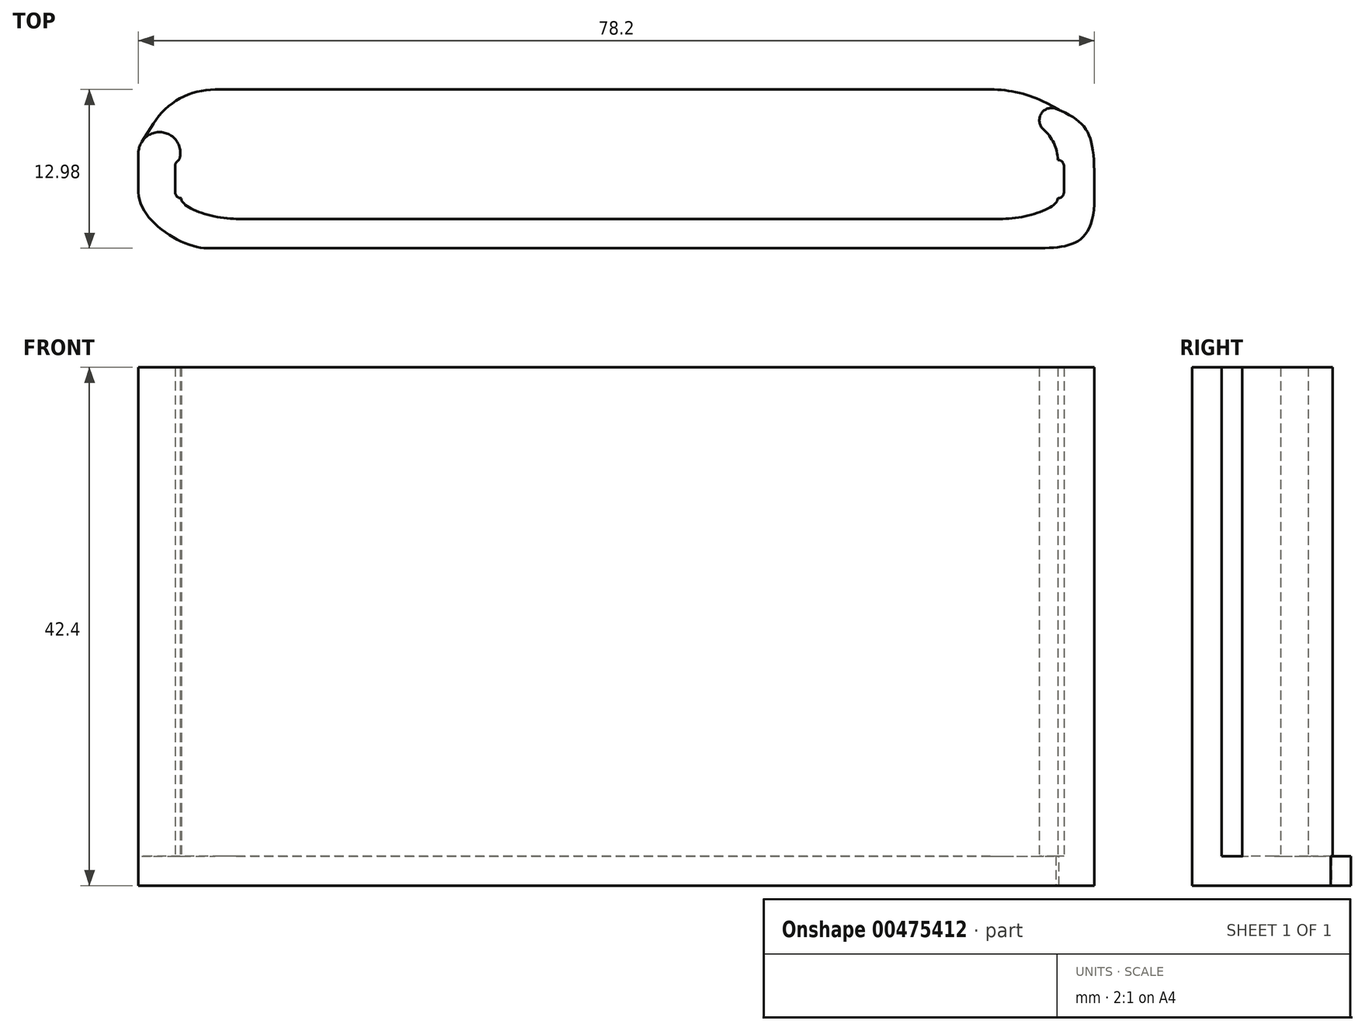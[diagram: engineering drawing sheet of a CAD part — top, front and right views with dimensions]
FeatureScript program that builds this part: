
annotation { "Feature Type Name" : "Feature", "Feature Type Description" : "" }
export const myFeature = defineFeature(function(context is Context, id is Id, definition is map)
    precondition{}
    {
        {
            var Q0;
            Q0=qCreatedBy(makeId("Top.planeOp"),FACE);
            var sketch = newSketch(context, id + "F0", { "sketchPlane" : qUnion([Q0])});
            skLineSegment(sketch, "E0", {"start": v(0, 15.59) * mm, "end": v(0, -8.36) * mm, "construction": true});
            skLineSegment(sketch, "E1", {"start": v(-58.12, 0) * mm, "end": v(52.13, 0) * mm, "construction": true});
            skLineSegment(sketch, "E2", {"start": v(0, 1.57) * mm, "end": v(35.85, 1.57) * mm});
            skLineSegment(sketch, "E3", {"start": v(36.35, 1.07) * mm, "end": v(36.35, -1.07) * mm});
            skLineSegment(sketch, "E4", {"start": v(35.85, -1.57) * mm, "end": v(0, -1.57) * mm});
            skLineSegment(sketch, "E5", {"start": v(0, 4.77) * mm, "end": v(31.35, 4.77) * mm});
            skPoint(sketch, "E6.visualSharp", {"position": v(36.35, 1.57) * mm});
            skArc(sketch, "E6.filletArc", {"start": v(36.35, 1.07) * mm, "mid": v(36.2, 1.42) * mm, "end": v(35.85, 1.57) * mm});
            skPoint(sketch, "E7.visualSharp", {"position": v(36.35, -1.57) * mm});
            skArc(sketch, "E7.filletArc", {"start": v(35.85, -1.57) * mm, "mid": v(36.2, -1.42) * mm, "end": v(36.35, -1.07) * mm});
            skLineSegment(sketch, "E8", {"start": v(0, -3.25) * mm, "end": v(31.35, -3.25) * mm});
            skLineSegment(sketch, "E9", {"start": v(35.85, 0) * mm, "end": v(35.85, 5.38) * mm, "construction": true});
            skLineSegment(sketch, "E10.MirrorCS", {"start": v(35.85, 0) * mm, "end": v(35.85, -5.38) * mm, "construction": true});
            skLineSegment(sketch, "E11.MirrorCS", {"start": v(0, 4.77) * mm, "end": v(-31.35, 4.77) * mm});
            skLineSegment(sketch, "E12.MirrorCS", {"start": v(0, 1.57) * mm, "end": v(-35.85, 1.57) * mm});
            skArc(sketch, "E13.MirrorCS", {"start": v(-36.35, 1.07) * mm, "mid": v(-36.3, 1.3) * mm, "end": v(-36.15, 1.47) * mm});
            skLineSegment(sketch, "E14.MirrorCS", {"start": v(-36.35, 1.07) * mm, "end": v(-36.35, -1.07) * mm});
            skArc(sketch, "E15.MirrorCS", {"start": v(-35.85, -1.57) * mm, "mid": v(-36.2, -1.42) * mm, "end": v(-36.35, -1.07) * mm});
            skLineSegment(sketch, "E16.MirrorCS", {"start": v(-35.85, -1.57) * mm, "end": v(0, -1.57) * mm});
            skLineSegment(sketch, "E17.MirrorCS", {"start": v(0, -3.25) * mm, "end": v(-31.35, -3.25) * mm});
            skPoint(sketch, "E18.middle", {"position": v(0, 0) * mm});
            skArc(sketch, "E19", {"start": v(35.71, 5.75) * mm, "mid": v(34.49, 5.35) * mm, "end": v(34.68, 4.07) * mm});
            skLineSegment(sketch, "E20.1", {"start": v(0, -5.65) * mm, "end": v(33.71, -5.65) * mm});
            skLineSegment(sketch, "E21", {"start": v(34.68, 4.07) * mm, "end": v(35.71, 5.75) * mm, "construction": true});
            skLineSegment(sketch, "E22.MirrorCS", {"start": v(0, -5.65) * mm, "end": v(-33.71, -5.65) * mm});
            skPoint(sketch, "E23.visualSharp", {"position": v(-35.85, 1.57) * mm});
            skLineSegment(sketch, "E24", {"start": v(-39.35, -1.07) * mm, "end": v(-39.35, 2.13) * mm});
            skArc(sketch, "E25", {"start": v(-35.95, 1.78) * mm, "mid": v(-37.46, 3.84) * mm, "end": v(-39.35, 2.13) * mm});
            skPoint(sketch, "E26.visualSharp", {"position": v(-36.02, 1.54) * mm});
            skArc(sketch, "E26.filletArc", {"start": v(-36.15, 1.47) * mm, "mid": v(-36.02, 1.6) * mm, "end": v(-35.95, 1.78) * mm});
            skFitSpline(sketch, "E27", {"points": [v(31.35, -3.25) * mm, v(35.85, -1.57) * mm], "startDerivative": vector(5.53, 0) * mm, "endDerivative": vector(0, 2.53) * mm});
            skFitSpline(sketch, "E28", {"points": [v(35.71, 5.75) * mm, v(38.85, -1.55) * mm], "startDerivative": vector(9.41, -3.77) * mm, "endDerivative": vector(0, -14.59) * mm});
            skFitSpline(sketch, "E29.MirrorCS", {"points": [v(-31.35, -3.25) * mm, v(-35.85, -1.57) * mm], "startDerivative": vector(-5.53, 0) * mm, "endDerivative": vector(0, 2.53) * mm});
            skFitSpline(sketch, "E30", {"points": [v(-39.35, -1.07) * mm, v(-33.71, -5.65) * mm], "startDerivative": vector(0, -7.12) * mm, "endDerivative": vector(6.13, 0) * mm});
            skFitSpline(sketch, "E31", {"points": [v(33.71, -5.65) * mm, v(38.85, -1.55) * mm], "startDerivative": vector(8.73, 0) * mm, "endDerivative": vector(0, 12.29) * mm});
            skArc(sketch, "E32", {"start": v(35.85, 1.57) * mm, "mid": v(34.4, 4.3) * mm, "end": v(31.35, 4.77) * mm});
            skArc(sketch, "E33.MirrorCS", {"start": v(-35.85, 1.57) * mm, "mid": v(-34.4, 4.3) * mm, "end": v(-31.35, 4.77) * mm});
            skPoint(sketch, "E34.newPointB", {"position": v(-38.71, 2.37) * mm});
            skSolve(sketch);
        }
        {
            var Q0;
            Q0=makeQuery(id+"F0.imprint","IMPRINT",FACE,{"disambiguationData":[TD([[makeQuery(id+"F0.imprint","IMPRINT",EDGE,{"derivedFrom":sQuery(id+"F0.wireOp",EDGE,"E3")}),1.0]])]});
            extrude(context, id + "F1", {"entities" : qUnion([Q0]), "depth" : 40 * mm});
        }
        {
            var Q0;
            Q0=makeQuery(id+"F1.opExtrude","CAP_FACE",FACE,{"disambiguationData":[OSD([sQuery(id+"F0.wireOp",EDGE,"E3"),sQuery(id+"F0.wireOp",EDGE,"E6.filletArc"),sQuery(id+"F0.wireOp",EDGE,"E7.filletArc"),sQuery(id+"F0.wireOp",EDGE,"E8"),sQuery(id+"F0.wireOp",EDGE,"E13.MirrorCS"),sQuery(id+"F0.wireOp",EDGE,"E14.MirrorCS"),sQuery(id+"F0.wireOp",EDGE,"E15.MirrorCS"),sQuery(id+"F0.wireOp",EDGE,"E17.MirrorCS"),sQuery(id+"F0.wireOp",EDGE,"E19"),sQuery(id+"F0.wireOp",EDGE,"E20.1"),sQuery(id+"F0.wireOp",EDGE,"E22.MirrorCS"),sQuery(id+"F0.wireOp",EDGE,"E24"),sQuery(id+"F0.wireOp",EDGE,"E25"),sQuery(id+"F0.wireOp",EDGE,"E26.filletArc"),sQuery(id+"F0.wireOp",EDGE,"E27"),sQuery(id+"F0.wireOp",EDGE,"E28"),sQuery(id+"F0.wireOp",EDGE,"E29.MirrorCS"),sQuery(id+"F0.wireOp",EDGE,"E30"),sQuery(id+"F0.wireOp",EDGE,"E31"),sQuery(id+"F0.wireOp",EDGE,"E32")])],"isStart":true});
            var sketch = newSketch(context, id + "F2", { "sketchPlane" : qUnion([Q0])});
            skLineSegment(sketch, "E35.0", {"start": v(33.71, 5.65) * mm, "end": v(-33.71, 5.65) * mm});
            skFitSpline(sketch, "E35.1", {"points": [v(33.71, 5.65) * mm, v(36.62, 5.65) * mm, v(38.85, 5.65) * mm, v(38.85, 1.55) * mm]});
            skFitSpline(sketch, "E35.2", {"points": [v(35.71, -5.75) * mm, v(38.85, -4.5) * mm, v(38.85, -3.3) * mm, v(38.85, 1.55) * mm]});
            skLineSegment(sketch, "E35.3", {"start": v(-39.35, 1.07) * mm, "end": v(-39.35, -2.13) * mm});
            skArc(sketch, "E35.4", {"start": v(-35.95, -1.78) * mm, "mid": v(-37.46, -3.84) * mm, "end": v(-39.35, -2.13) * mm});
            skFitSpline(sketch, "E35.5", {"points": [v(-39.35, 1.07) * mm, v(-39.35, 3.44) * mm, v(-35.75, 5.65) * mm, v(-33.71, 5.65) * mm]});
            skLineSegment(sketch, "E36", {"start": v(-45.92, 0) * mm, "end": v(41.33, 0) * mm, "construction": true});
            skLineSegment(sketch, "E37", {"start": v(0, 12.42) * mm, "end": v(0, -11.88) * mm, "construction": true});
            skArc(sketch, "E38.0", {"start": v(-35.85, -1.57) * mm, "mid": v(-34.4, -4.3) * mm, "end": v(-31.35, -4.77) * mm});
            skArc(sketch, "E39.0", {"start": v(35.85, -1.57) * mm, "mid": v(34.4, -4.3) * mm, "end": v(31.35, -4.77) * mm});
            skLineSegment(sketch, "E40", {"start": v(-32.4, -4.93) * mm, "end": v(32.4, -4.93) * mm});
            skArc(sketch, "E41.0", {"start": v(35.71, -5.75) * mm, "mid": v(34.49, -5.35) * mm, "end": v(34.68, -4.07) * mm});
            skLineSegment(sketch, "E42", {"start": v(30.34, -7.33) * mm, "end": v(-33.06, -7.33) * mm});
            skLineSegment(sketch, "E43", {"start": v(36.63, -5.34) * mm, "end": v(34.93, -6.22) * mm});
            skArc(sketch, "E44.filletArc", {"start": v(30.34, -7.33) * mm, "mid": v(32.7, -7.05) * mm, "end": v(34.93, -6.22) * mm});
            skLineSegment(sketch, "E45", {"start": v(-39.08, -3.05) * mm, "end": v(-38.13, -4.55) * mm});
            skArc(sketch, "E46.filletArc", {"start": v(-38.13, -4.55) * mm, "mid": v(-35.95, -6.6) * mm, "end": v(-33.06, -7.33) * mm});
            skSolve(sketch);
        }
        {
            var Q0;
            {var subQ2=sQuery(id+"F2.wireOp",EDGE,"E41.0");Q0=makeQuery(id+"F2.imprint","IMPRINT",FACE,{"disambiguationData":[TD([[makeQuery(id+"F2.imprint","IMPRINT",EDGE,{"derivedFrom":subQ2}),1.0]])]});}
            var Q1;
            Q1=makeQuery(id+"F0.imprint","IMPRINT",FACE,{"disambiguationData":[TD([[makeQuery(id+"F0.imprint","IMPRINT",EDGE,{"derivedFrom":sQuery(id+"F0.wireOp",EDGE,"E3")}),1.0]])]});
            extrude(context, id + "F3", {"entities" : qUnion([Q0, Q1]), "operationType" : NewBodyOperationType.ADD, "depth" : 2.4 * mm});
        }
    });
